# Revit family: Casement_38_F_Side_Hung_Standard
name_source: partatom
category: Windows
revit_build: Autodesk Revit 2014 (Build: 20130308_1515(x64)
units: mm (PartAtom-declared; Revit-internal decimal feet)

## types (12) — shared parameters
Aluminium Thickness = 1 mm  [stored 0.00328084 ft]
Area Pane Left Top = 0.52 m²
Area Pane Right Top = 0.52 m²
Bead SG Gap = 13 mm  [stored 0.0426509 ft]
Casement Dimension = 38 mm  [stored 0.124672 ft]
Custom Sash Left Height = 1154 mm  [stored 3.78609 ft]
Custom Sash Left Width = 554 mm  [stored 1.81759 ft]
Custom Sash Right Height = 1154 mm  [stored 3.78609 ft]
Custom Sash Right Width = 554 mm  [stored 1.81759 ft]
DG Extrusion Start = 9 mm  [stored 0.0295276 ft]
DG Gasket Finish = Double Glazing Gasket Material
DG Thickness Calc = 4 mm  [stored 0.0131234 ft]
Default Sill Height = 800 mm  [stored 2.62467 ft]
Depth Bead = 24 mm  [stored 0.0787402 ft]
Description = Window 38mm, Type F side hung
Frame Center Offset = 19 mm  [stored 0.062336 ft]
Height Sash Left = 1124 mm
Height Sash Left Opening = 1154 mm  [stored 3.78609 ft]
Height Sash Right = 1124 mm
Height Sash Right Opening = 1154 mm  [stored 3.78609 ft]
Length Transom Left = 540 mm  [stored 1.77165 ft]
Length Transom Right = 540 mm  [stored 1.77165 ft]
Limit Fixed Pane Height Max = 1800 mm
Limit Fixed Pane Height Min = 200 mm  [stored 0.656168 ft]
Limit Fixed Pane Width Max = 1500 mm
Limit Fixed Pane Width Min = 200 mm  [stored 0.656168 ft]
Limit Sash Height Max = 1500 mm
Limit Sash Height Min = 300 mm  [stored 0.984252 ft]
Limit Sash Width Max = 700 mm  [stored 2.29659 ft]
Limit Sash Width Min = 300 mm  [stored 0.984252 ft]
Limit Window Height Max = 1860 mm
Limit Window Height Min = 1430 mm  [stored 4.6916 ft]
Limit Window Width Max = 2700 mm
Limit Window Width Min = 1400 mm
Manufacturer = Crealco
Max System DG One Piece Thickness = 6 mm  [stored 0.019685 ft]
Max System DG Unit Thickness = 25 mm  [stored 0.082021 ft]
Model = Casement 38
Offset Bead Center Reversed = 19 mm  [stored 0.062336 ft]
Offset Fixed Panel Center Left = 600 mm  [stored 1.9685 ft]
Offset Mullion Left = 570 mm  [stored 1.87008 ft]
Offset Mullion Right = 570 mm  [stored 1.87008 ft]
Offset Sash Side = 23 mm  [stored 0.0754593 ft]
Offset Sash Top = 23 mm  [stored 0.0754593 ft]
Offset Transom Left Top = 1170 mm
Offset Transom Right Top = 1170 mm
Offset Window Exterior = 19 mm  [stored 0.062336 ft]
SG Gasket Thickness = 6 mm  [stored 0.019685 ft]
Sash Center Offset = 16 mm  [stored 0.0524934 ft]
Sash Overlap = 7 mm  [stored 0.0229659 ft]
Sash Spacing Inner = 8 mm  [stored 0.0262467 ft]
Side Hung Left = Yes
Side Hung Right = No
URL = http://www.crealco.co.za
Wall Closure = By host
Width Bead = 15 mm  [stored 0.0492126 ft]
Width Fixed Panel Left = 540 mm  [stored 1.77165 ft]
Width Fixed Panel Right = 540 mm  [stored 1.77165 ft]
Width Profile = 30 mm  [stored 0.0984252 ft]
Width Sash Left = 524 mm  [stored 1.71916 ft]
Width Sash Left Opening = 554 mm  [stored 1.81759 ft]
Width Sash Right = 524 mm  [stored 1.71916 ft]
Width Sash Right Opening = 554 mm  [stored 1.81759 ft]
zero-valued in all types: Corrected Mullion Size, Standard Mullion Different, Window Exterior Offset

## per-type parameters (varying)
- 38-1815SS-1000Pa: Area Pane Left Bottom=0.13 m²; Area Pane Middle=0.82 m²; Area Pane Right Bottom=0.13 m²; Clearvue Insulated LowE SHGC Value=0.546; Clearvue Insulated LowE U Value=3.62; Clearvue Insulated SHGC Value=0.6; Clearvue Insulated U Value=4.19; Clearvue SHGC Value=0.686; Clearvue U Value=6.66; Custom Windload=1000 mm  [stored 3.28084 ft]; Custom Window Height=1490 mm  [stored 4.88845 ft]; Custom Window Width=1790 mm; Depth Mullion=39 mm  [stored 0.127953 ft]; Energy Advantage SHGC Value=0.615; Energy Advantage U Value=4.94; Height=1490 mm  [stored 4.88845 ft]; Height Fixed Panel Center=1430 mm  [stored 4.6916 ft]; Height Fixed Panel Left=260 mm; Height Fixed Panel Right=260 mm; Intruderprufe Insulated LowE SHGC Value=0.505; Intruderprufe Insulated LowE U Value=3.54; Intruderprufe Insulated SHGC Value=0.554; Intruderprufe Insulated U Value=4.1; Intruderprufe LowE SHGC Value=0.574; Intruderprufe LowE U Value=4.81; Intruderprufe SHGC Value=0.669; Intruderprufe U Value=6.53; Length Mullion=1490 mm  [stored 4.88845 ft]; Max Pane Area=0.82 m²; Mullion Depth Windload Based=39 mm  [stored 0.127953 ft]; Width=1790 mm; Width Fixed Panel Center=590 mm; Windload Design=1000 mm  [stored 3.28084 ft]
- 38-1815SS-1500Pa: Area Pane Left Bottom=0.13 m²; Area Pane Middle=0.82 m²; Area Pane Right Bottom=0.13 m²; Clearvue Insulated LowE SHGC Value=0.547; Clearvue Insulated LowE U Value=3.69; Clearvue Insulated SHGC Value=0.601; Clearvue Insulated U Value=4.27; Clearvue SHGC Value=0.685; Clearvue U Value=6.66; Custom Windload=1500 mm; Custom Window Height=1490 mm  [stored 4.88845 ft]; Custom Window Width=1790 mm; Depth Mullion=54 mm  [stored 0.177165 ft]; Energy Advantage SHGC Value=0.613; Energy Advantage U Value=5.02; Height=1490 mm  [stored 4.88845 ft]; Height Fixed Panel Center=1430 mm  [stored 4.6916 ft]; Height Fixed Panel Left=260 mm; Height Fixed Panel Right=260 mm; Intruderprufe Insulated LowE SHGC Value=0.508; Intruderprufe Insulated LowE U Value=3.61; Intruderprufe Insulated SHGC Value=0.558; Intruderprufe Insulated U Value=4.17; Intruderprufe LowE SHGC Value=0.579; Intruderprufe LowE U Value=4.9; Intruderprufe SHGC Value=0.652; Intruderprufe U Value=6.56; Length Mullion=1490 mm  [stored 4.88845 ft]; Max Pane Area=0.82 m²; Mullion Depth Windload Based=54 mm  [stored 0.177165 ft]; Width=1790 mm; Width Fixed Panel Center=590 mm; Windload Design=1500 mm
- 38-1815SS-2000Pa: Area Pane Left Bottom=0.13 m²; Area Pane Middle=0.82 m²; Area Pane Right Bottom=0.13 m²; Clearvue Insulated LowE SHGC Value=0.547; Clearvue Insulated LowE U Value=3.69; Clearvue Insulated SHGC Value=0.601; Clearvue Insulated U Value=4.27; Clearvue SHGC Value=0.685; Clearvue U Value=6.66; Custom Windload=2000 mm; Custom Window Height=1490 mm  [stored 4.88845 ft]; Custom Window Width=1790 mm; Depth Mullion=54 mm  [stored 0.177165 ft]; Energy Advantage SHGC Value=0.613; Energy Advantage U Value=5.02; Height=1490 mm  [stored 4.88845 ft]; Height Fixed Panel Center=1430 mm  [stored 4.6916 ft]; Height Fixed Panel Left=260 mm; Height Fixed Panel Right=260 mm; Intruderprufe Insulated LowE SHGC Value=0.508; Intruderprufe Insulated LowE U Value=3.61; Intruderprufe Insulated SHGC Value=0.558; Intruderprufe Insulated U Value=4.17; Intruderprufe LowE SHGC Value=0.579; Intruderprufe LowE U Value=4.9; Intruderprufe SHGC Value=0.652; Intruderprufe U Value=6.56; Length Mullion=1490 mm  [stored 4.88845 ft]; Max Pane Area=0.82 m²; Mullion Depth Windload Based=54 mm  [stored 0.177165 ft]; Width=1790 mm; Width Fixed Panel Center=590 mm; Windload Design=2000 mm
- 38-2415SS-1000Pa: Area Pane Left Bottom=0.13 m²; Area Pane Middle=1.68 m²; Area Pane Right Bottom=0.13 m²; Clearvue Insulated LowE SHGC Value=0.603; Clearvue Insulated LowE U Value=3.5; Clearvue Insulated SHGC Value=0.663; Clearvue Insulated U Value=4.16; Clearvue SHGC Value=0; Clearvue U Value=7.9; Custom Windload=1000 mm  [stored 3.28084 ft]; Custom Window Height=1490 mm  [stored 4.88845 ft]; Custom Window Width=2390 mm; Depth Mullion=54 mm  [stored 0.177165 ft]; Energy Advantage SHGC Value=0; Energy Advantage U Value=7.9; Height=1490 mm  [stored 4.88845 ft]; Height Fixed Panel Center=1430 mm  [stored 4.6916 ft]; Height Fixed Panel Left=260 mm; Height Fixed Panel Right=260 mm; Intruderprufe Insulated LowE SHGC Value=0.558; Intruderprufe Insulated LowE U Value=3.43; Intruderprufe Insulated SHGC Value=0.615; Intruderprufe Insulated U Value=4.06; Intruderprufe LowE SHGC Value=0.633; Intruderprufe LowE U Value=4.88; Intruderprufe SHGC Value=0.717; Intruderprufe U Value=6.71; Length Mullion=1490 mm  [stored 4.88845 ft]; Max Pane Area=1.68 m²; Mullion Depth Windload Based=54 mm  [stored 0.177165 ft]; Width=2390 mm; Width Fixed Panel Center=1190 mm  [stored 3.9042 ft]; Windload Design=1000 mm  [stored 3.28084 ft]
- 38-2415SS-1500Pa: Area Pane Left Bottom=0.13 m²; Area Pane Middle=1.68 m²; Area Pane Right Bottom=0.13 m²; Clearvue Insulated LowE SHGC Value=0.603; Clearvue Insulated LowE U Value=3.5; Clearvue Insulated SHGC Value=0.663; Clearvue Insulated U Value=4.16; Clearvue SHGC Value=0; Clearvue U Value=7.9; Custom Windload=1500 mm; Custom Window Height=1490 mm  [stored 4.88845 ft]; Custom Window Width=2390 mm; Depth Mullion=54 mm  [stored 0.177165 ft]; Energy Advantage SHGC Value=0; Energy Advantage U Value=7.9; Height=1490 mm  [stored 4.88845 ft]; Height Fixed Panel Center=1430 mm  [stored 4.6916 ft]; Height Fixed Panel Left=260 mm; Height Fixed Panel Right=260 mm; Intruderprufe Insulated LowE SHGC Value=0.558; Intruderprufe Insulated LowE U Value=3.43; Intruderprufe Insulated SHGC Value=0.615; Intruderprufe Insulated U Value=4.06; Intruderprufe LowE SHGC Value=0.633; Intruderprufe LowE U Value=4.88; Intruderprufe SHGC Value=0.717; Intruderprufe U Value=6.71; Length Mullion=1490 mm  [stored 4.88845 ft]; Max Pane Area=1.68 m²; Mullion Depth Windload Based=54 mm  [stored 0.177165 ft]; Width=2390 mm; Width Fixed Panel Center=1190 mm  [stored 3.9042 ft]; Windload Design=1500 mm
- 38-2415SS-2000Pa: Area Pane Left Bottom=0.13 m²; Area Pane Middle=1.68 m²; Area Pane Right Bottom=0.13 m²; Clearvue Insulated LowE SHGC Value=0.605; Clearvue Insulated LowE U Value=3.6; Clearvue Insulated SHGC Value=0.665; Clearvue Insulated U Value=4.25; Clearvue SHGC Value=0; Clearvue U Value=7.9; Custom Windload=2000 mm; Custom Window Height=1490 mm  [stored 4.88845 ft]; Custom Window Width=2390 mm; Depth Mullion=70 mm  [stored 0.229659 ft]; Energy Advantage SHGC Value=0; Energy Advantage U Value=7.9; Height=1490 mm  [stored 4.88845 ft]; Height Fixed Panel Center=1430 mm  [stored 4.6916 ft]; Height Fixed Panel Left=260 mm; Height Fixed Panel Right=260 mm; Intruderprufe Insulated LowE SHGC Value=0.559; Intruderprufe Insulated LowE U Value=3.52; Intruderprufe Insulated SHGC Value=0.615; Intruderprufe Insulated U Value=4.15; Intruderprufe LowE SHGC Value=0.634; Intruderprufe LowE U Value=5; Intruderprufe SHGC Value=0.704; Intruderprufe U Value=6.73; Length Mullion=1490 mm  [stored 4.88845 ft]; Max Pane Area=1.68 m²; Mullion Depth Windload Based=70 mm  [stored 0.229659 ft]; Width=2390 mm; Width Fixed Panel Center=1190 mm  [stored 3.9042 ft]; Windload Design=2000 mm
- 38-1818SS-1000Pa: Area Pane Left Bottom=0.29 m²; Area Pane Middle=1 m²; Area Pane Right Bottom=0.29 m²; Clearvue Insulated LowE SHGC Value=0.589; Clearvue Insulated LowE U Value=3.76; Clearvue Insulated SHGC Value=0.647; Clearvue Insulated U Value=4.39; Clearvue SHGC Value=0.737; Clearvue U Value=6.697; Custom Windload=1000 mm  [stored 3.28084 ft]; Custom Window Height=1790 mm; Custom Window Width=1790 mm; Depth Mullion=54 mm  [stored 0.177165 ft]; Energy Advantage SHGC Value=0.66; Energy Advantage U Value=5.21; Height=1790 mm; Height Fixed Panel Center=1730 mm; Height Fixed Panel Left=560 mm; Height Fixed Panel Right=560 mm; Intruderprufe Insulated LowE SHGC Value=0.545; Intruderprufe Insulated LowE U Value=3.68; Intruderprufe Insulated SHGC Value=0.6; Intruderprufe Insulated U Value=4.29; Intruderprufe LowE SHGC Value=0.619; Intruderprufe LowE U Value=5.08; Intruderprufe SHGC Value=0.7; Intruderprufe U Value=6.86; Length Mullion=1790 mm; Max Pane Area=1 m²; Mullion Depth Windload Based=54 mm  [stored 0.177165 ft]; Width=1790 mm; Width Fixed Panel Center=590 mm; Windload Design=1000 mm  [stored 3.28084 ft]
- 38-1818SS-1500Pa: Area Pane Left Bottom=0.29 m²; Area Pane Middle=1 m²; Area Pane Right Bottom=0.29 m²; Clearvue Insulated LowE SHGC Value=0.591; Clearvue Insulated LowE U Value=3.89; Clearvue Insulated SHGC Value=0.649; Clearvue Insulated U Value=4.51; Clearvue SHGC Value=0.736; Clearvue U Value=6.87; Custom Windload=1500 mm; Custom Window Height=1790 mm; Custom Window Width=1790 mm; Depth Mullion=70 mm  [stored 0.229659 ft]; Energy Advantage SHGC Value=0.662; Energy Advantage U Value=5.36; Height=1790 mm; Height Fixed Panel Center=1730 mm; Height Fixed Panel Left=560 mm; Height Fixed Panel Right=560 mm; Intruderprufe Insulated LowE SHGC Value=0.546; Intruderprufe Insulated LowE U Value=3.8; Intruderprufe Insulated SHGC Value=0.6; Intruderprufe Insulated U Value=4.4; Intruderprufe LowE SHGC Value=0.62; Intruderprufe LowE U Value=5.24; Intruderprufe SHGC Value=0.684; Intruderprufe U Value=6.88; Length Mullion=1790 mm; Max Pane Area=1 m²; Mullion Depth Windload Based=70 mm  [stored 0.229659 ft]; Width=1790 mm; Width Fixed Panel Center=590 mm; Windload Design=1500 mm
- 38-1818SS-2000Pa: Area Pane Left Bottom=0.29 m²; Area Pane Middle=1 m²; Area Pane Right Bottom=0.29 m²; Clearvue Insulated LowE SHGC Value=0.591; Clearvue Insulated LowE U Value=3.89; Clearvue Insulated SHGC Value=0.649; Clearvue Insulated U Value=4.51; Clearvue SHGC Value=0.736; Clearvue U Value=6.87; Custom Windload=2000 mm; Custom Window Height=1790 mm; Custom Window Width=1790 mm; Depth Mullion=70 mm  [stored 0.229659 ft]; Energy Advantage SHGC Value=0.662; Energy Advantage U Value=5.36; Height=1790 mm; Height Fixed Panel Center=1730 mm; Height Fixed Panel Left=560 mm; Height Fixed Panel Right=560 mm; Intruderprufe Insulated LowE SHGC Value=0.546; Intruderprufe Insulated LowE U Value=3.8; Intruderprufe Insulated SHGC Value=0.6; Intruderprufe Insulated U Value=4.4; Intruderprufe LowE SHGC Value=0.62; Intruderprufe LowE U Value=5.24; Intruderprufe SHGC Value=0.684; Intruderprufe U Value=6.88; Length Mullion=1790 mm; Max Pane Area=1 m²; Mullion Depth Windload Based=70 mm  [stored 0.229659 ft]; Width=1790 mm; Width Fixed Panel Center=590 mm; Windload Design=2000 mm
- 38-2418SS-1000Pa: Area Pane Left Bottom=0.29 m²; Area Pane Middle=2.03 m²; Area Pane Right Bottom=0.29 m²; Clearvue Insulated LowE SHGC Value=0.667; Clearvue Insulated LowE U Value=3.77; Clearvue Insulated SHGC Value=0.733; Clearvue Insulated U Value=4.5; Clearvue SHGC Value=0; Clearvue U Value=7.9; Custom Windload=1000 mm  [stored 3.28084 ft]; Custom Window Height=1790 mm; Custom Window Width=2390 mm; Depth Mullion=70 mm  [stored 0.229659 ft]; Energy Advantage SHGC Value=0; Energy Advantage U Value=7.9; Height=1790 mm; Height Fixed Panel Center=1730 mm; Height Fixed Panel Left=560 mm; Height Fixed Panel Right=560 mm; Intruderprufe Insulated LowE SHGC Value=0.615; Intruderprufe Insulated LowE U Value=3.7; Intruderprufe Insulated SHGC Value=0.679; Intruderprufe Insulated U Value=4.39; Intruderprufe LowE SHGC Value=0.698; Intruderprufe LowE U Value=5.33; Intruderprufe SHGC Value=0.777; Intruderprufe U Value=7.25; Length Mullion=1790 mm; Max Pane Area=2.03 m²; Mullion Depth Windload Based=70 mm  [stored 0.229659 ft]; Width=2390 mm; Width Fixed Panel Center=1190 mm  [stored 3.9042 ft]; Windload Design=1000 mm  [stored 3.28084 ft]
- 38-2418SS-1500Pa: Area Pane Left Bottom=0.29 m²; Area Pane Middle=2.03 m²; Area Pane Right Bottom=0.29 m²; Clearvue Insulated LowE SHGC Value=0.667; Clearvue Insulated LowE U Value=3.77; Clearvue Insulated SHGC Value=0.733; Clearvue Insulated U Value=4.5; Clearvue SHGC Value=0; Clearvue U Value=7.9; Custom Windload=1500 mm; Custom Window Height=1790 mm; Custom Window Width=2390 mm; Depth Mullion=70 mm  [stored 0.229659 ft]; Energy Advantage SHGC Value=0; Energy Advantage U Value=7.9; Height=1790 mm; Height Fixed Panel Center=1730 mm; Height Fixed Panel Left=560 mm; Height Fixed Panel Right=560 mm; Intruderprufe Insulated LowE SHGC Value=0.615; Intruderprufe Insulated LowE U Value=3.7; Intruderprufe Insulated SHGC Value=0.679; Intruderprufe Insulated U Value=4.39; Intruderprufe LowE SHGC Value=0.698; Intruderprufe LowE U Value=5.33; Intruderprufe SHGC Value=0.777; Intruderprufe U Value=7.25; Length Mullion=1790 mm; Max Pane Area=2.03 m²; Mullion Depth Windload Based=70 mm  [stored 0.229659 ft]; Width=2390 mm; Width Fixed Panel Center=1190 mm  [stored 3.9042 ft]; Windload Design=1500 mm
- 38-2418SS-2000Pa: Area Pane Left Bottom=0.29 m²; Area Pane Middle=2.03 m²; Area Pane Right Bottom=0.29 m²; Clearvue Insulated LowE SHGC Value=0.667; Clearvue Insulated LowE U Value=3.77; Clearvue Insulated SHGC Value=0.733; Clearvue Insulated U Value=4.5; Clearvue SHGC Value=0; Clearvue U Value=7.9; Custom Windload=2000 mm; Custom Window Height=1790 mm; Custom Window Width=2390 mm; Depth Mullion=76 mm  [stored 0.249344 ft]; Energy Advantage SHGC Value=0; Energy Advantage U Value=7.9; Height=1790 mm; Height Fixed Panel Center=1730 mm; Height Fixed Panel Left=560 mm; Height Fixed Panel Right=560 mm; Intruderprufe Insulated LowE SHGC Value=0.615; Intruderprufe Insulated LowE U Value=3.7; Intruderprufe Insulated SHGC Value=0.679; Intruderprufe Insulated U Value=4.39; Intruderprufe LowE SHGC Value=0.698; Intruderprufe LowE U Value=5.33; Intruderprufe SHGC Value=0.777; Intruderprufe U Value=7.25; Length Mullion=1790 mm; Max Pane Area=2.03 m²; Mullion Depth Windload Based=76 mm  [stored 0.249344 ft]; Width=2390 mm; Width Fixed Panel Center=1190 mm  [stored 3.9042 ft]; Windload Design=2000 mm

note: [stored X ft] marks values corroborated as IEEE doubles in the binary element streams (Revit-internal decimal feet)

## geometry (parser evidence)
native form markers: Extrusion x1, Sweep x29
no freeform markers — native parametric forms only
